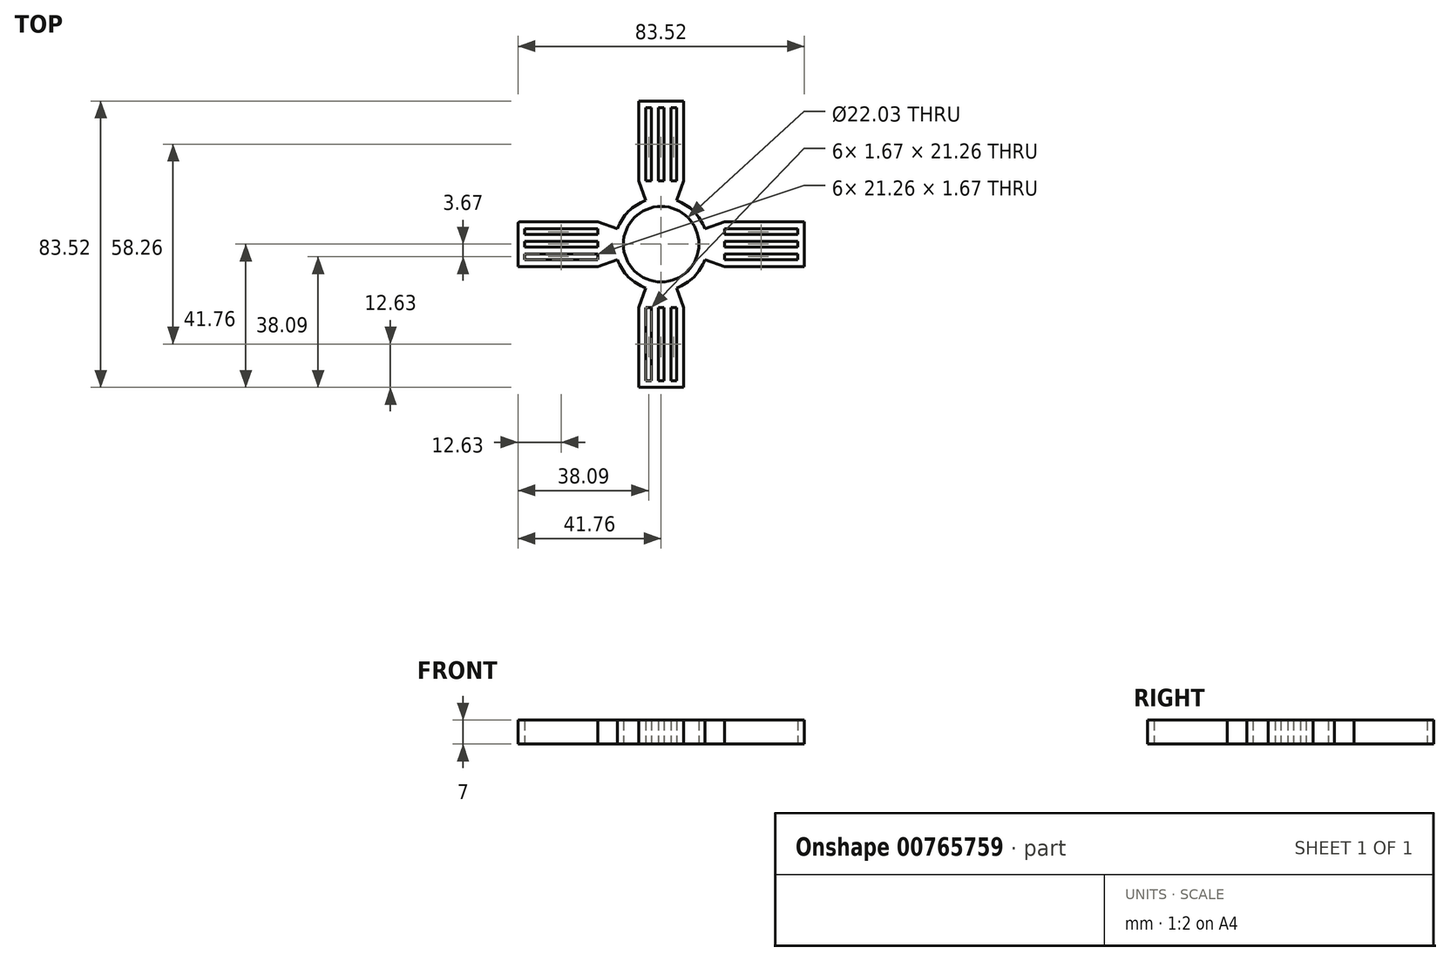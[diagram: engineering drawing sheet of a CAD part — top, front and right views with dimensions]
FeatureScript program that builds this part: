
annotation { "Feature Type Name" : "Feature", "Feature Type Description" : "" }
export const myFeature = defineFeature(function(context is Context, id is Id, definition is map)
    precondition{}
    {
        {
            var Q0;
            Q0=qCreatedBy(makeId("Top.planeOp"),FACE);
            var sketch = newSketch(context, id + "F0", { "sketchPlane" : qUnion([Q0])});
            skCircle(sketch, "E0", {"center": v(0, 0) * mm, "radius": 11.02 * mm});
            skCircle(sketch, "E1", {"center": v(0, 0) * mm, "radius": 13.5 * mm});
            skLineSegment(sketch, "E2", {"start": v(0, 13.5) * mm, "end": v(0, 18.5) * mm});
            skLineSegment(sketch, "E3", {"start": v(0, 18.5) * mm, "end": v(0.83, 18.5) * mm});
            skLineSegment(sketch, "E4", {"start": v(0.83, 18.5) * mm, "end": v(0.83, 39.76) * mm});
            skLineSegment(sketch, "E5", {"start": v(0.83, 18.5) * mm, "end": v(2.83, 18.5) * mm});
            skLineSegment(sketch, "E6", {"start": v(2.83, 18.5) * mm, "end": v(2.83, 39.76) * mm});
            skLineSegment(sketch, "E7", {"start": v(2.83, 39.76) * mm, "end": v(0.83, 39.76) * mm});
            skLineSegment(sketch, "E8", {"start": v(2.83, 18.5) * mm, "end": v(4.5, 18.5) * mm});
            skLineSegment(sketch, "E9", {"start": v(4.5, 18.5) * mm, "end": v(4.5, 39.76) * mm});
            skLineSegment(sketch, "E10", {"start": v(4.5, 39.76) * mm, "end": v(2.83, 39.76) * mm});
            skLineSegment(sketch, "E11", {"start": v(4.5, 39.76) * mm, "end": v(6.5, 39.76) * mm});
            skLineSegment(sketch, "E12", {"start": v(6.5, 39.76) * mm, "end": v(6.5, 18.5) * mm});
            skLineSegment(sketch, "E13", {"start": v(6.5, 18.5) * mm, "end": v(4.48, 12.74) * mm});
            skLineSegment(sketch, "E14", {"start": v(0.83, 39.76) * mm, "end": v(0, 39.76) * mm});
            skLineSegment(sketch, "E15.MirrorCS", {"start": v(-0.83, 18.5) * mm, "end": v(-0.83, 39.76) * mm});
            skLineSegment(sketch, "E16.MirrorCS", {"start": v(-2.83, 18.5) * mm, "end": v(-2.83, 39.76) * mm});
            skLineSegment(sketch, "E17.MirrorCS", {"start": v(-4.5, 18.5) * mm, "end": v(-4.5, 39.76) * mm});
            skLineSegment(sketch, "E18.MirrorCS", {"start": v(-6.5, 39.76) * mm, "end": v(-6.5, 18.5) * mm});
            skLineSegment(sketch, "E19.MirrorCS", {"start": v(-6.5, 18.5) * mm, "end": v(-4.48, 12.74) * mm});
            skLineSegment(sketch, "E20.MirrorCS", {"start": v(-2.83, 39.76) * mm, "end": v(-0.83, 39.76) * mm});
            skLineSegment(sketch, "E21.MirrorCS", {"start": v(-4.5, 39.76) * mm, "end": v(-2.83, 39.76) * mm});
            skLineSegment(sketch, "E22.MirrorCS", {"start": v(-4.5, 39.76) * mm, "end": v(-6.5, 39.76) * mm});
            skLineSegment(sketch, "E23.MirrorCS", {"start": v(-0.83, 18.5) * mm, "end": v(-2.83, 18.5) * mm});
            skLineSegment(sketch, "E24.MirrorCS", {"start": v(-2.83, 18.5) * mm, "end": v(-4.5, 18.5) * mm});
            skLineSegment(sketch, "E25", {"start": v(-6.5, 39.76) * mm, "end": v(-6.5, 41.76) * mm});
            skLineSegment(sketch, "E26", {"start": v(-6.5, 41.76) * mm, "end": v(6.5, 41.76) * mm});
            skLineSegment(sketch, "E27", {"start": v(6.5, 41.76) * mm, "end": v(6.5, 39.76) * mm});
            skLineSegment(sketch, "E28", {"start": v(-0.83, 18.5) * mm, "end": v(0.83, 18.5) * mm});
            skLineSegment(sketch, "E29", {"start": v(-0.83, 39.76) * mm, "end": v(0.83, 39.76) * mm});
            skLineSegment(sketch, "E30.1.0", {"start": v(-18.5, -6.5) * mm, "end": v(-12.74, -4.48) * mm});
            skLineSegment(sketch, "E30.1.1", {"start": v(-18.5, -4.5) * mm, "end": v(-39.76, -4.5) * mm});
            skLineSegment(sketch, "E30.1.2", {"start": v(-18.5, 2.84) * mm, "end": v(-39.76, 2.84) * mm});
            skLineSegment(sketch, "E30.1.3", {"start": v(-18.5, 0.84) * mm, "end": v(-39.76, 0.84) * mm});
            skLineSegment(sketch, "E30.1.4", {"start": v(-18.5, 4.5) * mm, "end": v(-39.76, 4.5) * mm});
            skLineSegment(sketch, "E30.1.5", {"start": v(-13.5, 0) * mm, "end": v(-18.5, 0) * mm});
            skLineSegment(sketch, "E30.1.6", {"start": v(-41.76, -6.5) * mm, "end": v(-41.76, 5.9) * mm});
            skLineSegment(sketch, "E30.1.7", {"start": v(-18.5, -2.83) * mm, "end": v(-39.76, -2.83) * mm});
            skLineSegment(sketch, "E30.1.8", {"start": v(-18.5, 6.5) * mm, "end": v(-12.74, 4.48) * mm});
            skLineSegment(sketch, "E30.1.9", {"start": v(-18.5, -0.83) * mm, "end": v(-39.76, -0.83) * mm});
            skLineSegment(sketch, "E30.1.10", {"start": v(-39.76, -6.5) * mm, "end": v(-18.5, -6.5) * mm});
            skLineSegment(sketch, "E30.1.11", {"start": v(-39.76, 6.5) * mm, "end": v(-18.5, 6.5) * mm});
            skLineSegment(sketch, "E30.1.12", {"start": v(-18.5, -4.5) * mm, "end": v(-39.76, -4.5) * mm});
            skLineSegment(sketch, "E30.1.13", {"start": v(-18.5, -0.83) * mm, "end": v(-39.76, -0.83) * mm});
            skLineSegment(sketch, "E30.1.14", {"start": v(-18.5, -2.83) * mm, "end": v(-39.76, -2.83) * mm});
            skLineSegment(sketch, "E30.1.15", {"start": v(-39.76, -6.5) * mm, "end": v(-18.5, -6.5) * mm});
            skLineSegment(sketch, "E30.1.16", {"start": v(-18.5, 2.84) * mm, "end": v(-18.5, 4.5) * mm});
            skLineSegment(sketch, "E30.1.17", {"start": v(-39.76, -6.5) * mm, "end": v(-41.76, -6.5) * mm});
            skLineSegment(sketch, "E30.1.18", {"start": v(-41.16, 6.5) * mm, "end": v(-39.76, 6.5) * mm});
            skLineSegment(sketch, "E30.1.19", {"start": v(-18.5, 0.84) * mm, "end": v(-18.5, 2.84) * mm});
            skLineSegment(sketch, "E30.1.20", {"start": v(-39.76, 2.84) * mm, "end": v(-39.76, 0.84) * mm});
            skLineSegment(sketch, "E30.1.21", {"start": v(-18.5, -2.83) * mm, "end": v(-18.5, -4.5) * mm});
            skLineSegment(sketch, "E30.1.22", {"start": v(-39.76, 4.5) * mm, "end": v(-39.76, 6.5) * mm});
            skLineSegment(sketch, "E30.1.23", {"start": v(-39.76, 4.5) * mm, "end": v(-39.76, 2.84) * mm});
            skLineSegment(sketch, "E30.1.24", {"start": v(-39.76, -4.5) * mm, "end": v(-39.76, -2.83) * mm});
            skLineSegment(sketch, "E30.1.25", {"start": v(-18.5, 0) * mm, "end": v(-18.5, 0.84) * mm});
            skLineSegment(sketch, "E30.1.26", {"start": v(-39.76, -4.5) * mm, "end": v(-39.76, -6.5) * mm});
            skLineSegment(sketch, "E30.1.27", {"start": v(-39.76, -0.83) * mm, "end": v(-39.76, 0.84) * mm});
            skLineSegment(sketch, "E30.1.28", {"start": v(-39.76, 0.84) * mm, "end": v(-39.76, 0) * mm});
            skLineSegment(sketch, "E30.1.29", {"start": v(-39.76, -2.83) * mm, "end": v(-39.76, -0.83) * mm});
            skLineSegment(sketch, "E30.1.30", {"start": v(-18.5, -0.83) * mm, "end": v(-18.5, 0.84) * mm});
            skLineSegment(sketch, "E30.1.31", {"start": v(-18.5, -0.83) * mm, "end": v(-18.5, -2.83) * mm});
            skLineSegment(sketch, "E30.2.0", {"start": v(6.5, -18.5) * mm, "end": v(4.48, -12.74) * mm});
            skLineSegment(sketch, "E30.2.1", {"start": v(4.5, -18.5) * mm, "end": v(4.5, -39.76) * mm});
            skLineSegment(sketch, "E30.2.2", {"start": v(-2.84, -18.5) * mm, "end": v(-2.84, -39.76) * mm});
            skLineSegment(sketch, "E30.2.3", {"start": v(-0.84, -18.5) * mm, "end": v(-0.84, -39.76) * mm});
            skLineSegment(sketch, "E30.2.4", {"start": v(-4.5, -18.5) * mm, "end": v(-4.5, -39.76) * mm});
            skLineSegment(sketch, "E30.2.5", {"start": v(0, -13.5) * mm, "end": v(0, -18.5) * mm});
            skLineSegment(sketch, "E30.2.6", {"start": v(6.5, -41.76) * mm, "end": v(-6.5, -41.76) * mm});
            skLineSegment(sketch, "E30.2.7", {"start": v(2.83, -18.5) * mm, "end": v(2.83, -39.76) * mm});
            skLineSegment(sketch, "E30.2.8", {"start": v(-6.5, -18.5) * mm, "end": v(-4.48, -12.74) * mm});
            skLineSegment(sketch, "E30.2.9", {"start": v(0.83, -18.5) * mm, "end": v(0.83, -39.76) * mm});
            skLineSegment(sketch, "E30.2.10", {"start": v(6.5, -39.76) * mm, "end": v(6.5, -18.5) * mm});
            skLineSegment(sketch, "E30.2.11", {"start": v(-6.5, -39.76) * mm, "end": v(-6.5, -18.5) * mm});
            skLineSegment(sketch, "E30.2.12", {"start": v(4.5, -18.5) * mm, "end": v(4.5, -39.76) * mm});
            skLineSegment(sketch, "E30.2.13", {"start": v(0.83, -18.5) * mm, "end": v(0.83, -39.76) * mm});
            skLineSegment(sketch, "E30.2.14", {"start": v(2.83, -18.5) * mm, "end": v(2.83, -39.76) * mm});
            skLineSegment(sketch, "E30.2.15", {"start": v(6.5, -39.76) * mm, "end": v(6.5, -18.5) * mm});
            skLineSegment(sketch, "E30.2.16", {"start": v(-2.84, -18.5) * mm, "end": v(-4.5, -18.5) * mm});
            skLineSegment(sketch, "E30.2.17", {"start": v(6.5, -39.76) * mm, "end": v(6.5, -41.76) * mm});
            skLineSegment(sketch, "E30.2.18", {"start": v(-6.5, -41.76) * mm, "end": v(-6.5, -39.76) * mm});
            skLineSegment(sketch, "E30.2.19", {"start": v(-0.84, -18.5) * mm, "end": v(-2.84, -18.5) * mm});
            skLineSegment(sketch, "E30.2.20", {"start": v(-2.84, -39.76) * mm, "end": v(-0.84, -39.76) * mm});
            skLineSegment(sketch, "E30.2.21", {"start": v(2.83, -18.5) * mm, "end": v(4.5, -18.5) * mm});
            skLineSegment(sketch, "E30.2.22", {"start": v(-4.5, -39.76) * mm, "end": v(-6.5, -39.76) * mm});
            skLineSegment(sketch, "E30.2.23", {"start": v(-4.5, -39.76) * mm, "end": v(-2.84, -39.76) * mm});
            skLineSegment(sketch, "E30.2.24", {"start": v(4.5, -39.76) * mm, "end": v(2.83, -39.76) * mm});
            skLineSegment(sketch, "E30.2.25", {"start": v(0, -18.5) * mm, "end": v(-0.84, -18.5) * mm});
            skLineSegment(sketch, "E30.2.26", {"start": v(4.5, -39.76) * mm, "end": v(6.5, -39.76) * mm});
            skLineSegment(sketch, "E30.2.27", {"start": v(0.83, -39.76) * mm, "end": v(-0.84, -39.76) * mm});
            skLineSegment(sketch, "E30.2.28", {"start": v(-0.84, -39.76) * mm, "end": v(0, -39.76) * mm});
            skLineSegment(sketch, "E30.2.29", {"start": v(2.83, -39.76) * mm, "end": v(0.83, -39.76) * mm});
            skLineSegment(sketch, "E30.2.30", {"start": v(0.83, -18.5) * mm, "end": v(-0.84, -18.5) * mm});
            skLineSegment(sketch, "E30.2.31", {"start": v(0.83, -18.5) * mm, "end": v(2.83, -18.5) * mm});
            skLineSegment(sketch, "E30.3.0", {"start": v(18.5, 6.5) * mm, "end": v(12.74, 4.48) * mm});
            skLineSegment(sketch, "E30.3.1", {"start": v(18.5, 4.5) * mm, "end": v(39.76, 4.5) * mm});
            skLineSegment(sketch, "E30.3.2", {"start": v(18.5, -2.84) * mm, "end": v(39.76, -2.84) * mm});
            skLineSegment(sketch, "E30.3.3", {"start": v(18.5, -0.84) * mm, "end": v(39.76, -0.84) * mm});
            skLineSegment(sketch, "E30.3.4", {"start": v(18.5, -4.5) * mm, "end": v(39.76, -4.5) * mm});
            skLineSegment(sketch, "E30.3.5", {"start": v(13.5, 0) * mm, "end": v(18.5, 0) * mm});
            skLineSegment(sketch, "E30.3.6", {"start": v(41.76, 6.5) * mm, "end": v(41.76, -6.5) * mm});
            skLineSegment(sketch, "E30.3.7", {"start": v(18.5, 2.83) * mm, "end": v(39.76, 2.83) * mm});
            skLineSegment(sketch, "E30.3.8", {"start": v(18.5, -6.5) * mm, "end": v(12.74, -4.48) * mm});
            skLineSegment(sketch, "E30.3.9", {"start": v(18.5, 0.83) * mm, "end": v(39.76, 0.83) * mm});
            skLineSegment(sketch, "E30.3.10", {"start": v(39.76, 6.5) * mm, "end": v(18.5, 6.5) * mm});
            skLineSegment(sketch, "E30.3.11", {"start": v(39.76, -6.5) * mm, "end": v(18.5, -6.5) * mm});
            skLineSegment(sketch, "E30.3.12", {"start": v(18.5, 4.5) * mm, "end": v(39.76, 4.5) * mm});
            skLineSegment(sketch, "E30.3.13", {"start": v(18.5, 0.83) * mm, "end": v(39.76, 0.83) * mm});
            skLineSegment(sketch, "E30.3.14", {"start": v(18.5, 2.83) * mm, "end": v(39.76, 2.83) * mm});
            skLineSegment(sketch, "E30.3.15", {"start": v(39.76, 6.5) * mm, "end": v(18.5, 6.5) * mm});
            skLineSegment(sketch, "E30.3.16", {"start": v(18.5, -2.84) * mm, "end": v(18.5, -4.5) * mm});
            skLineSegment(sketch, "E30.3.17", {"start": v(39.76, 6.5) * mm, "end": v(41.76, 6.5) * mm});
            skLineSegment(sketch, "E30.3.18", {"start": v(41.76, -6.5) * mm, "end": v(39.76, -6.5) * mm});
            skLineSegment(sketch, "E30.3.19", {"start": v(18.5, -0.84) * mm, "end": v(18.5, -2.84) * mm});
            skLineSegment(sketch, "E30.3.20", {"start": v(39.76, -2.84) * mm, "end": v(39.76, -0.84) * mm});
            skLineSegment(sketch, "E30.3.21", {"start": v(18.5, 2.83) * mm, "end": v(18.5, 4.5) * mm});
            skLineSegment(sketch, "E30.3.22", {"start": v(39.76, -4.5) * mm, "end": v(39.76, -6.5) * mm});
            skLineSegment(sketch, "E30.3.23", {"start": v(39.76, -4.5) * mm, "end": v(39.76, -2.84) * mm});
            skLineSegment(sketch, "E30.3.24", {"start": v(39.76, 4.5) * mm, "end": v(39.76, 2.83) * mm});
            skLineSegment(sketch, "E30.3.25", {"start": v(18.5, 0) * mm, "end": v(18.5, -0.84) * mm});
            skLineSegment(sketch, "E30.3.26", {"start": v(39.76, 4.5) * mm, "end": v(39.76, 6.5) * mm});
            skLineSegment(sketch, "E30.3.27", {"start": v(39.76, 0.83) * mm, "end": v(39.76, -0.84) * mm});
            skLineSegment(sketch, "E30.3.28", {"start": v(39.76, -0.84) * mm, "end": v(39.76, 0) * mm});
            skLineSegment(sketch, "E30.3.29", {"start": v(39.76, 2.83) * mm, "end": v(39.76, 0.83) * mm});
            skLineSegment(sketch, "E30.3.30", {"start": v(18.5, 0.83) * mm, "end": v(18.5, -0.84) * mm});
            skLineSegment(sketch, "E30.3.31", {"start": v(18.5, 0.83) * mm, "end": v(18.5, 2.83) * mm});
            skPoint(sketch, "E31.visualSharp", {"position": v(-41.76, 6.5) * mm});
            skArc(sketch, "E31.filletArc", {"start": v(-41.16, 6.5) * mm, "mid": v(-41.58, 6.33) * mm, "end": v(-41.76, 5.9) * mm});
            skSolve(sketch);
        }
        {
            var Q0;
            {var subQ6=sQuery(id+"F0.wireOp",EDGE,"E30.1.0");var subQ16=sQuery(id+"F0.wireOp",EDGE,"E2");var subQ19=sQuery(id+"F0.wireOp",EDGE,"E30.3.0");var subQ27=sQuery(id+"F0.wireOp",EDGE,"E30.2.0");var subQ56=makeQuery(id+"F0.imprint","IMPRINT",EDGE,{"derivedFrom":subQ16});Q0=qUnion([makeQuery(id+"F0.imprint","IMPRINT",FACE,{"disambiguationData":[TD([[makeQuery(id+"F0.imprint","IMPRINT",EDGE,{"derivedFrom":subQ19}),1.0]])]}),makeQuery(id+"F0.imprint","IMPRINT",FACE,{"disambiguationData":[TD([[subQ56,-1.0]])]}),makeQuery(id+"F0.imprint","IMPRINT",FACE,{"disambiguationData":[TD([[subQ56,1.0]])]}),makeQuery(id+"F0.imprint","IMPRINT",FACE,{"disambiguationData":[TD([[makeQuery(id+"F0.imprint","IMPRINT",EDGE,{"derivedFrom":sQuery(id+"F0.wireOp",EDGE,"E30.1.4")}),-1.0]])]}),makeQuery(id+"F0.imprint","IMPRINT",FACE,{"disambiguationData":[TD([[makeQuery(id+"F0.imprint","IMPRINT",EDGE,{"derivedFrom":subQ6}),1.0]])]}),makeQuery(id+"F0.imprint","IMPRINT",FACE,{"disambiguationData":[TD([[makeQuery(id+"F0.imprint","IMPRINT",EDGE,{"derivedFrom":sQuery(id+"F0.wireOp",EDGE,"E30.2.4")}),-1.0]])]}),makeQuery(id+"F0.imprint","IMPRINT",FACE,{"disambiguationData":[TD([[makeQuery(id+"F0.imprint","IMPRINT",EDGE,{"derivedFrom":subQ27}),1.0]])]}),makeQuery(id+"F0.imprint","IMPRINT",FACE,{"disambiguationData":[TD([[makeQuery(id+"F0.imprint","IMPRINT",EDGE,{"derivedFrom":sQuery(id+"F0.wireOp",EDGE,"E30.3.4")}),-1.0]])]}),makeQuery(id+"F0.imprint","IMPRINT",FACE,{"disambiguationData":[TD([[makeQuery(id+"F0.imprint","IMPRINT",EDGE,{"derivedFrom":sQuery(id+"F0.wireOp",EDGE,"E7")}),-1.0]])]}),makeQuery(id+"F0.imprint","IMPRINT",FACE,{"disambiguationData":[TD([[makeQuery(id+"F0.imprint","IMPRINT",EDGE,{"derivedFrom":sQuery(id+"F0.wireOp",EDGE,"E30.1.6")}),-1.0]])]}),makeQuery(id+"F0.imprint","IMPRINT",FACE,{"disambiguationData":[TD([[makeQuery(id+"F0.imprint","IMPRINT",EDGE,{"derivedFrom":sQuery(id+"F0.wireOp",EDGE,"E30.2.6")}),-1.0]])]}),makeQuery(id+"F0.imprint","IMPRINT",FACE,{"disambiguationData":[TD([[makeQuery(id+"F0.imprint","IMPRINT",EDGE,{"derivedFrom":sQuery(id+"F0.wireOp",EDGE,"E30.3.6")}),-1.0]])]}),makeQuery(id+"F0.imprint","IMPRINT",FACE,{"disambiguationData":[TD([[makeQuery(id+"F0.imprint","IMPRINT",EDGE,{"derivedFrom":sQuery(id+"F0.wireOp",EDGE,"E0")}),-1.0]])]})]);}
            extrude(context, id + "F1", {"entities" : qUnion([Q0]), "depth" : 7 * mm, "offsetDistance" : 25 * mm});
        }
        {
            var Q0;
            {var subQ6=sQuery(id+"F0.wireOp",EDGE,"E30.1.0");var subQ16=sQuery(id+"F0.wireOp",EDGE,"E2");var subQ19=sQuery(id+"F0.wireOp",EDGE,"E30.3.0");var subQ27=sQuery(id+"F0.wireOp",EDGE,"E30.2.0");var subQ56=makeQuery(id+"F0.imprint","IMPRINT",EDGE,{"derivedFrom":subQ16});Q0=qUnion([makeQuery(id+"F0.imprint","IMPRINT",FACE,{"disambiguationData":[TD([[makeQuery(id+"F0.imprint","IMPRINT",EDGE,{"derivedFrom":subQ19}),1.0]])]}),makeQuery(id+"F0.imprint","IMPRINT",FACE,{"disambiguationData":[TD([[subQ56,-1.0]])]}),makeQuery(id+"F0.imprint","IMPRINT",FACE,{"disambiguationData":[TD([[subQ56,1.0]])]}),makeQuery(id+"F0.imprint","IMPRINT",FACE,{"disambiguationData":[TD([[makeQuery(id+"F0.imprint","IMPRINT",EDGE,{"derivedFrom":sQuery(id+"F0.wireOp",EDGE,"E30.1.4")}),-1.0]])]}),makeQuery(id+"F0.imprint","IMPRINT",FACE,{"disambiguationData":[TD([[makeQuery(id+"F0.imprint","IMPRINT",EDGE,{"derivedFrom":subQ6}),1.0]])]}),makeQuery(id+"F0.imprint","IMPRINT",FACE,{"disambiguationData":[TD([[makeQuery(id+"F0.imprint","IMPRINT",EDGE,{"derivedFrom":sQuery(id+"F0.wireOp",EDGE,"E30.2.4")}),-1.0]])]}),makeQuery(id+"F0.imprint","IMPRINT",FACE,{"disambiguationData":[TD([[makeQuery(id+"F0.imprint","IMPRINT",EDGE,{"derivedFrom":subQ27}),1.0]])]}),makeQuery(id+"F0.imprint","IMPRINT",FACE,{"disambiguationData":[TD([[makeQuery(id+"F0.imprint","IMPRINT",EDGE,{"derivedFrom":sQuery(id+"F0.wireOp",EDGE,"E30.3.4")}),-1.0]])]}),makeQuery(id+"F0.imprint","IMPRINT",FACE,{"disambiguationData":[TD([[makeQuery(id+"F0.imprint","IMPRINT",EDGE,{"derivedFrom":sQuery(id+"F0.wireOp",EDGE,"E7")}),-1.0]])]}),makeQuery(id+"F0.imprint","IMPRINT",FACE,{"disambiguationData":[TD([[makeQuery(id+"F0.imprint","IMPRINT",EDGE,{"derivedFrom":sQuery(id+"F0.wireOp",EDGE,"E30.1.6")}),-1.0]])]}),makeQuery(id+"F0.imprint","IMPRINT",FACE,{"disambiguationData":[TD([[makeQuery(id+"F0.imprint","IMPRINT",EDGE,{"derivedFrom":sQuery(id+"F0.wireOp",EDGE,"E30.2.6")}),-1.0]])]}),makeQuery(id+"F0.imprint","IMPRINT",FACE,{"disambiguationData":[TD([[makeQuery(id+"F0.imprint","IMPRINT",EDGE,{"derivedFrom":sQuery(id+"F0.wireOp",EDGE,"E30.3.6")}),-1.0]])]}),makeQuery(id+"F0.imprint","IMPRINT",FACE,{"disambiguationData":[TD([[makeQuery(id+"F0.imprint","IMPRINT",EDGE,{"derivedFrom":sQuery(id+"F0.wireOp",EDGE,"E0")}),-1.0]])]})]);}
            extrude(context, id + "F2", {"entities" : qUnion([Q0]), "operationType" : NewBodyOperationType.ADD, "depth" : 7 * mm, "offsetDistance" : 25 * mm});
        }
        {
            var Q0;
            {var subQ6=sQuery(id+"F0.wireOp",EDGE,"E30.1.0");var subQ16=sQuery(id+"F0.wireOp",EDGE,"E2");var subQ19=sQuery(id+"F0.wireOp",EDGE,"E30.3.0");var subQ27=sQuery(id+"F0.wireOp",EDGE,"E30.2.0");var subQ56=makeQuery(id+"F0.imprint","IMPRINT",EDGE,{"derivedFrom":subQ16});Q0=qUnion([makeQuery(id+"F0.imprint","IMPRINT",FACE,{"disambiguationData":[TD([[makeQuery(id+"F0.imprint","IMPRINT",EDGE,{"derivedFrom":subQ19}),1.0]])]}),makeQuery(id+"F0.imprint","IMPRINT",FACE,{"disambiguationData":[TD([[subQ56,-1.0]])]}),makeQuery(id+"F0.imprint","IMPRINT",FACE,{"disambiguationData":[TD([[subQ56,1.0]])]}),makeQuery(id+"F0.imprint","IMPRINT",FACE,{"disambiguationData":[TD([[makeQuery(id+"F0.imprint","IMPRINT",EDGE,{"derivedFrom":sQuery(id+"F0.wireOp",EDGE,"E30.1.4")}),-1.0]])]}),makeQuery(id+"F0.imprint","IMPRINT",FACE,{"disambiguationData":[TD([[makeQuery(id+"F0.imprint","IMPRINT",EDGE,{"derivedFrom":subQ6}),1.0]])]}),makeQuery(id+"F0.imprint","IMPRINT",FACE,{"disambiguationData":[TD([[makeQuery(id+"F0.imprint","IMPRINT",EDGE,{"derivedFrom":sQuery(id+"F0.wireOp",EDGE,"E30.2.4")}),-1.0]])]}),makeQuery(id+"F0.imprint","IMPRINT",FACE,{"disambiguationData":[TD([[makeQuery(id+"F0.imprint","IMPRINT",EDGE,{"derivedFrom":subQ27}),1.0]])]}),makeQuery(id+"F0.imprint","IMPRINT",FACE,{"disambiguationData":[TD([[makeQuery(id+"F0.imprint","IMPRINT",EDGE,{"derivedFrom":sQuery(id+"F0.wireOp",EDGE,"E30.3.4")}),-1.0]])]}),makeQuery(id+"F0.imprint","IMPRINT",FACE,{"disambiguationData":[TD([[makeQuery(id+"F0.imprint","IMPRINT",EDGE,{"derivedFrom":sQuery(id+"F0.wireOp",EDGE,"E7")}),-1.0]])]}),makeQuery(id+"F0.imprint","IMPRINT",FACE,{"disambiguationData":[TD([[makeQuery(id+"F0.imprint","IMPRINT",EDGE,{"derivedFrom":sQuery(id+"F0.wireOp",EDGE,"E30.1.6")}),-1.0]])]}),makeQuery(id+"F0.imprint","IMPRINT",FACE,{"disambiguationData":[TD([[makeQuery(id+"F0.imprint","IMPRINT",EDGE,{"derivedFrom":sQuery(id+"F0.wireOp",EDGE,"E30.2.6")}),-1.0]])]}),makeQuery(id+"F0.imprint","IMPRINT",FACE,{"disambiguationData":[TD([[makeQuery(id+"F0.imprint","IMPRINT",EDGE,{"derivedFrom":sQuery(id+"F0.wireOp",EDGE,"E30.3.6")}),-1.0]])]}),makeQuery(id+"F0.imprint","IMPRINT",FACE,{"disambiguationData":[TD([[makeQuery(id+"F0.imprint","IMPRINT",EDGE,{"derivedFrom":sQuery(id+"F0.wireOp",EDGE,"E0")}),-1.0]])]})]);}
            extrude(context, id + "F3", {"entities" : qUnion([Q0]), "operationType" : NewBodyOperationType.ADD, "depth" : 7 * mm, "offsetDistance" : 25 * mm});
        }
        {
            var Q0;
            {var subQ6=sQuery(id+"F0.wireOp",EDGE,"E30.1.0");var subQ16=sQuery(id+"F0.wireOp",EDGE,"E2");var subQ19=sQuery(id+"F0.wireOp",EDGE,"E30.3.0");var subQ27=sQuery(id+"F0.wireOp",EDGE,"E30.2.0");var subQ56=makeQuery(id+"F0.imprint","IMPRINT",EDGE,{"derivedFrom":subQ16});Q0=qUnion([makeQuery(id+"F0.imprint","IMPRINT",FACE,{"disambiguationData":[TD([[makeQuery(id+"F0.imprint","IMPRINT",EDGE,{"derivedFrom":subQ19}),1.0]])]}),makeQuery(id+"F0.imprint","IMPRINT",FACE,{"disambiguationData":[TD([[subQ56,-1.0]])]}),makeQuery(id+"F0.imprint","IMPRINT",FACE,{"disambiguationData":[TD([[subQ56,1.0]])]}),makeQuery(id+"F0.imprint","IMPRINT",FACE,{"disambiguationData":[TD([[makeQuery(id+"F0.imprint","IMPRINT",EDGE,{"derivedFrom":sQuery(id+"F0.wireOp",EDGE,"E30.1.4")}),-1.0]])]}),makeQuery(id+"F0.imprint","IMPRINT",FACE,{"disambiguationData":[TD([[makeQuery(id+"F0.imprint","IMPRINT",EDGE,{"derivedFrom":subQ6}),1.0]])]}),makeQuery(id+"F0.imprint","IMPRINT",FACE,{"disambiguationData":[TD([[makeQuery(id+"F0.imprint","IMPRINT",EDGE,{"derivedFrom":sQuery(id+"F0.wireOp",EDGE,"E30.2.4")}),-1.0]])]}),makeQuery(id+"F0.imprint","IMPRINT",FACE,{"disambiguationData":[TD([[makeQuery(id+"F0.imprint","IMPRINT",EDGE,{"derivedFrom":subQ27}),1.0]])]}),makeQuery(id+"F0.imprint","IMPRINT",FACE,{"disambiguationData":[TD([[makeQuery(id+"F0.imprint","IMPRINT",EDGE,{"derivedFrom":sQuery(id+"F0.wireOp",EDGE,"E30.3.4")}),-1.0]])]}),makeQuery(id+"F0.imprint","IMPRINT",FACE,{"disambiguationData":[TD([[makeQuery(id+"F0.imprint","IMPRINT",EDGE,{"derivedFrom":sQuery(id+"F0.wireOp",EDGE,"E7")}),-1.0]])]}),makeQuery(id+"F0.imprint","IMPRINT",FACE,{"disambiguationData":[TD([[makeQuery(id+"F0.imprint","IMPRINT",EDGE,{"derivedFrom":sQuery(id+"F0.wireOp",EDGE,"E30.1.6")}),-1.0]])]}),makeQuery(id+"F0.imprint","IMPRINT",FACE,{"disambiguationData":[TD([[makeQuery(id+"F0.imprint","IMPRINT",EDGE,{"derivedFrom":sQuery(id+"F0.wireOp",EDGE,"E30.2.6")}),-1.0]])]}),makeQuery(id+"F0.imprint","IMPRINT",FACE,{"disambiguationData":[TD([[makeQuery(id+"F0.imprint","IMPRINT",EDGE,{"derivedFrom":sQuery(id+"F0.wireOp",EDGE,"E30.3.6")}),-1.0]])]}),makeQuery(id+"F0.imprint","IMPRINT",FACE,{"disambiguationData":[TD([[makeQuery(id+"F0.imprint","IMPRINT",EDGE,{"derivedFrom":sQuery(id+"F0.wireOp",EDGE,"E0")}),-1.0]])]})]);}
            var Q1;
            Q1=makeQuery(id+"F0.imprint","IMPRINT",FACE,{"disambiguationData":[TD([[makeQuery(id+"F0.imprint","IMPRINT",EDGE,{"derivedFrom":sQuery(id+"F0.wireOp",EDGE,"E15.MirrorCS")}),1.0]])]});
            var Q2;
            Q2=makeQuery(id+"F0.imprint","IMPRINT",FACE,{"disambiguationData":[TD([[makeQuery(id+"F0.imprint","IMPRINT",EDGE,{"derivedFrom":sQuery(id+"F0.wireOp",EDGE,"E4")}),-1.0]])]});
            var Q3;
            Q3=makeQuery(id+"F0.imprint","IMPRINT",FACE,{"disambiguationData":[TD([[makeQuery(id+"F0.imprint","IMPRINT",EDGE,{"derivedFrom":sQuery(id+"F0.wireOp",EDGE,"E30.3.7")}),-1.0]])]});
            var Q4;
            Q4=makeQuery(id+"F0.imprint","IMPRINT",FACE,{"disambiguationData":[TD([[makeQuery(id+"F0.imprint","IMPRINT",EDGE,{"derivedFrom":sQuery(id+"F0.wireOp",EDGE,"E30.3.2")}),1.0]])]});
            var Q5;
            Q5=makeQuery(id+"F0.imprint","IMPRINT",FACE,{"disambiguationData":[TD([[makeQuery(id+"F0.imprint","IMPRINT",EDGE,{"derivedFrom":sQuery(id+"F0.wireOp",EDGE,"E30.1.2")}),1.0]])]});
            var Q6;
            Q6=makeQuery(id+"F0.imprint","IMPRINT",FACE,{"disambiguationData":[TD([[makeQuery(id+"F0.imprint","IMPRINT",EDGE,{"derivedFrom":sQuery(id+"F0.wireOp",EDGE,"E30.1.7")}),-1.0]])]});
            var Q7;
            Q7=makeQuery(id+"F0.imprint","IMPRINT",FACE,{"disambiguationData":[TD([[makeQuery(id+"F0.imprint","IMPRINT",EDGE,{"derivedFrom":sQuery(id+"F0.wireOp",EDGE,"E30.2.2")}),1.0]])]});
            var Q8;
            Q8=makeQuery(id+"F0.imprint","IMPRINT",FACE,{"disambiguationData":[TD([[makeQuery(id+"F0.imprint","IMPRINT",EDGE,{"derivedFrom":sQuery(id+"F0.wireOp",EDGE,"E30.2.7")}),-1.0]])]});
            extrude(context, id + "F4", {"entities" : qUnion([Q0, Q1, Q2, Q3, Q4, Q5, Q6, Q7, Q8]), "operationType" : NewBodyOperationType.ADD, "depth" : 7 * mm, "offsetDistance" : 25 * mm});
        }
    });
